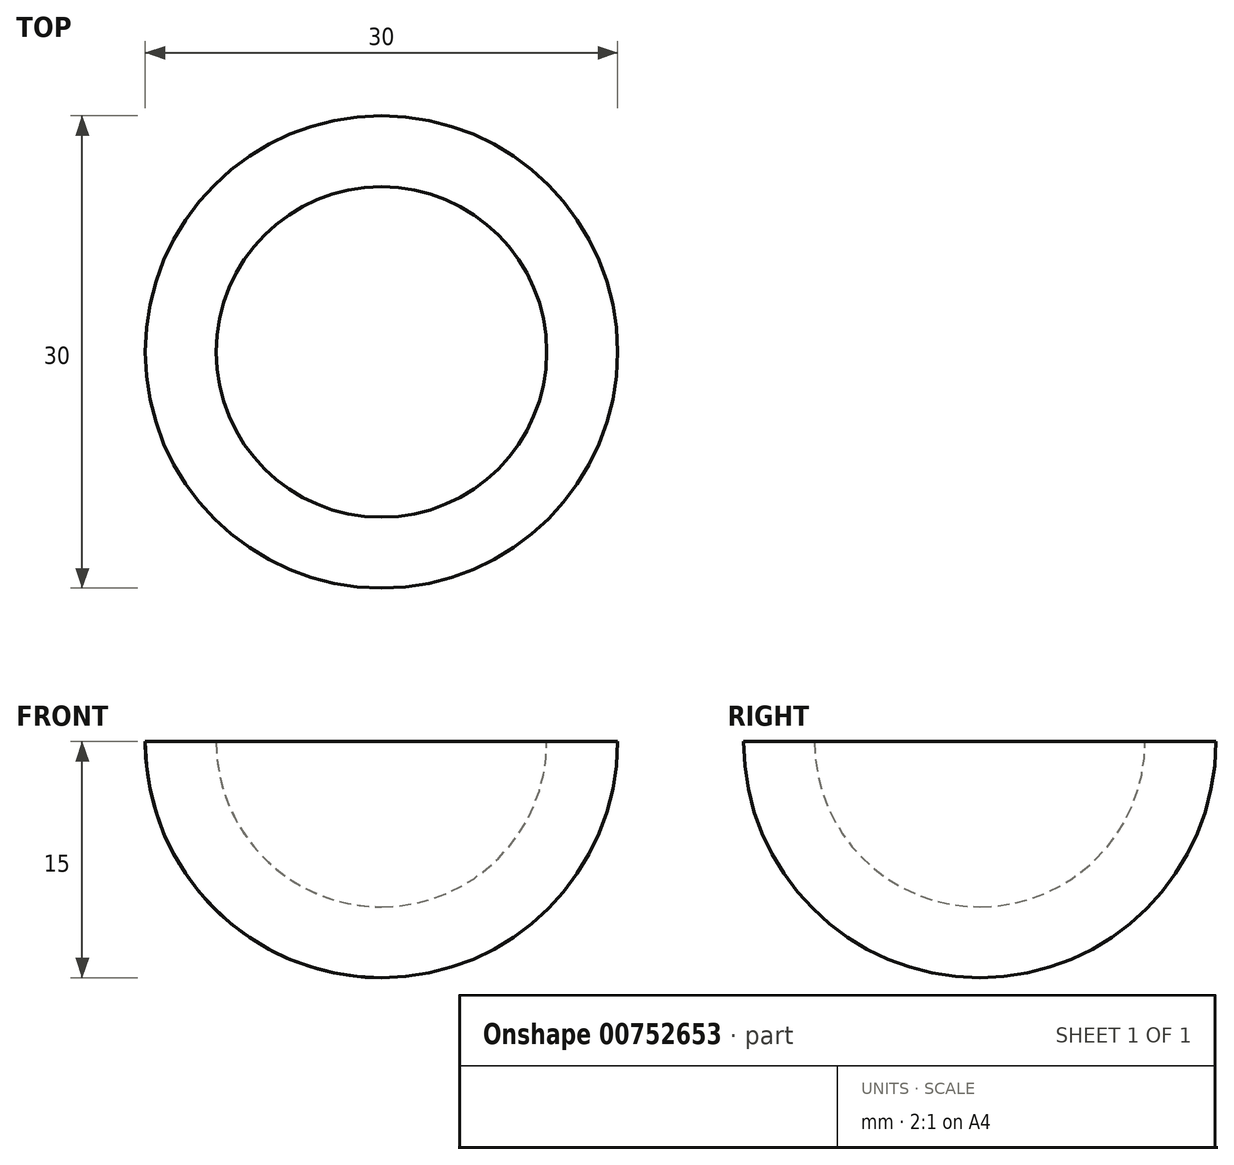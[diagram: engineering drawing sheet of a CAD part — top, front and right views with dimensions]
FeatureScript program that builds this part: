
annotation { "Feature Type Name" : "Feature", "Feature Type Description" : "" }
export const myFeature = defineFeature(function(context is Context, id is Id, definition is map)
    precondition{}
    {
        {
            var Q0;
            Q0=qCreatedBy(makeId("Front.planeOp"),FACE);
            var sketch = newSketch(context, id + "F0", { "sketchPlane" : qUnion([Q0])});
            skArc(sketch, "E0", {"start": v(0, -10.5) * mm, "mid": v(7.42, -7.42) * mm, "end": v(10.5, 0) * mm});
            skLineSegment(sketch, "E1", {"start": v(0, -10.5) * mm, "end": v(0, 0) * mm});
            skArc(sketch, "E2", {"start": v(0, -15) * mm, "mid": v(10.6, -10.6) * mm, "end": v(15, 0) * mm});
            skLineSegment(sketch, "E3", {"start": v(0, 0) * mm, "end": v(10.5, 0) * mm});
            skLineSegment(sketch, "E4", {"start": v(0, -10.5) * mm, "end": v(0, -15) * mm});
            skLineSegment(sketch, "E5", {"start": v(10.5, 0) * mm, "end": v(15, 0) * mm});
            skSolve(sketch);
        }
        {
            var Q0;
            Q0=qCreatedBy(makeId("Top.planeOp"),FACE);
            var sketch = newSketch(context, id + "F1", { "sketchPlane" : qUnion([Q0])});
            skCircle(sketch, "E6", {"center": v(0, 0) * mm, "radius": 10 * mm, "construction": true});
            skSolve(sketch);
        }
        {
            var Q0;
            Q0=makeQuery(id+"F0.imprint","IMPRINT",FACE,{"disambiguationData":[TD([[makeQuery(id+"F0.imprint","IMPRINT",EDGE,{"derivedFrom":sQuery(id+"F0.wireOp",EDGE,"E0")}),-1.0]])]});
            var Q1;
            Q1=sQuery(id+"F1.wireOp",EDGE,"E6");
            revolve(context, id + "F2", {"entities" : qUnion([Q0]), "axis" : qUnion([Q1]), "revolveType" : RevolveType.FULL});
        }
    });
